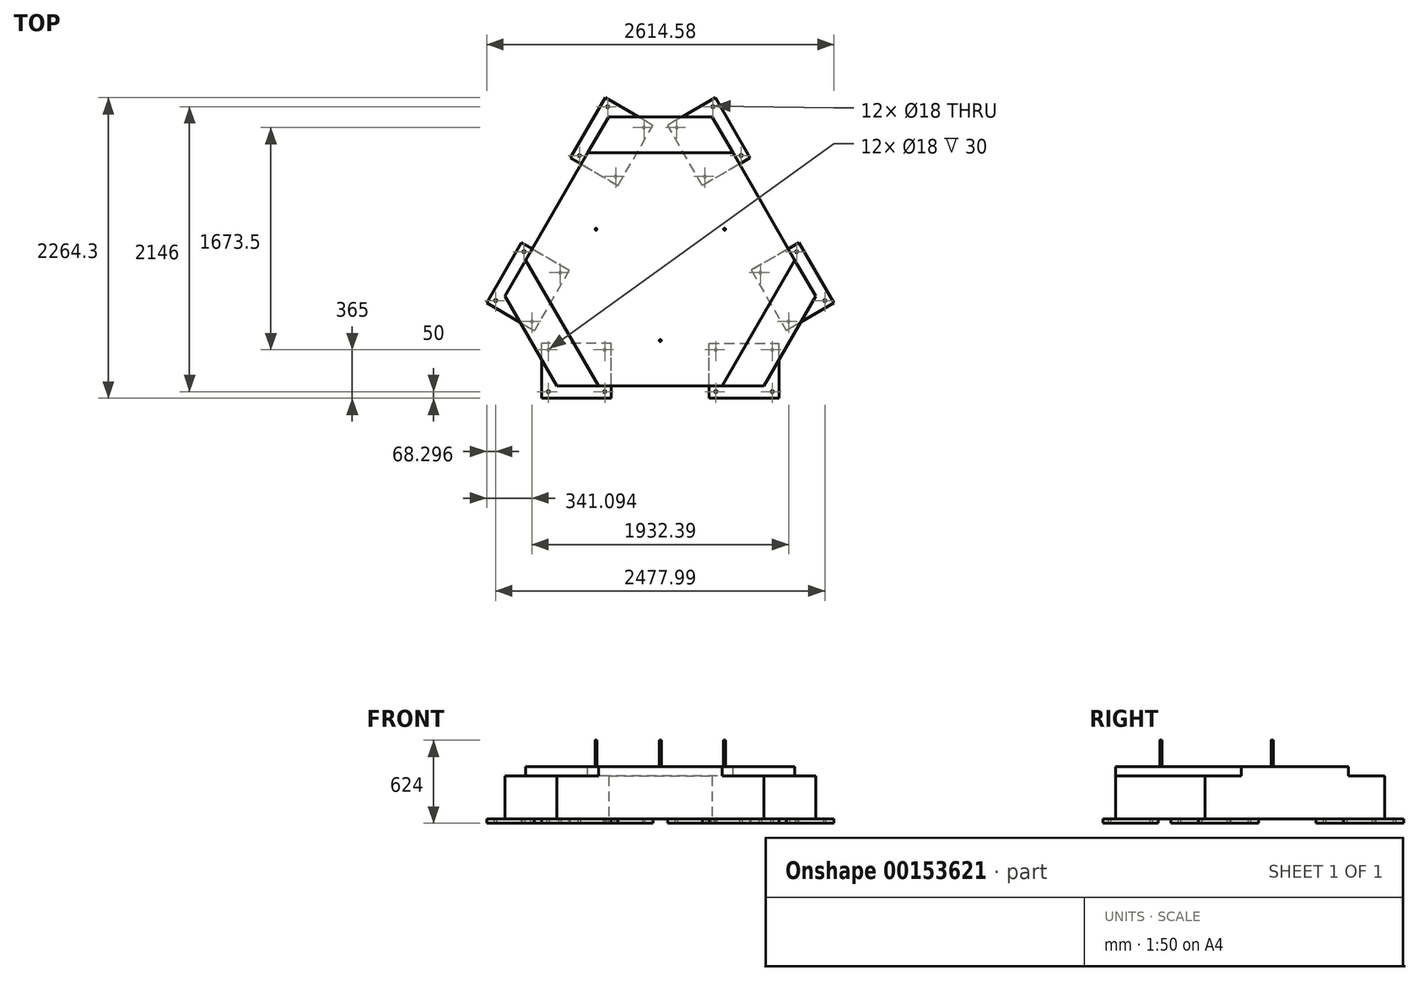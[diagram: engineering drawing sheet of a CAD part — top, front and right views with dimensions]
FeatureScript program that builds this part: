
annotation { "Feature Type Name" : "Feature", "Feature Type Description" : "" }
export const myFeature = defineFeature(function(context is Context, id is Id, definition is map)
    precondition{}
    {
        {
            var Q0;
            Q0=qCreatedBy(makeId("Top.planeOp"),FACE);
            var sketch = newSketch(context, id + "F0", { "sketchPlane" : qUnion([Q0])});
            skLineSegment(sketch, "E0", {"start": v(0, 1125.83) * mm, "end": v(390, 1125.83) * mm});
            skLineSegment(sketch, "E1", {"start": v(390, 1125.83) * mm, "end": v(780, 450.33) * mm});
            skLineSegment(sketch, "E2", {"start": v(0, 1304.98) * mm, "end": v(0, 0) * mm, "construction": true});
            skLineSegment(sketch, "E3", {"start": v(0, 0) * mm, "end": v(-698.78, -403.44) * mm, "construction": true});
            skLineSegment(sketch, "E4", {"start": v(0, 0) * mm, "end": v(965.92, -557.68) * mm, "construction": true});
            skLineSegment(sketch, "E5.MirrorCS", {"start": v(0, 1125.83) * mm, "end": v(-390, 1125.83) * mm});
            skLineSegment(sketch, "E6.MirrorCS", {"start": v(-390, 1125.83) * mm, "end": v(-780, 450.33) * mm});
            skLineSegment(sketch, "E7.MirrorCS", {"start": v(975, -562.92) * mm, "end": v(780, -900.67) * mm});
            skLineSegment(sketch, "E8.MirrorCS", {"start": v(975, -562.92) * mm, "end": v(1170, -225.17) * mm});
            skLineSegment(sketch, "E9.MirrorCS", {"start": v(1170, -225.17) * mm, "end": v(780, 450.33) * mm});
            skLineSegment(sketch, "E10.MirrorCS", {"start": v(780, -900.67) * mm, "end": v(0, -900.67) * mm});
            skLineSegment(sketch, "E11.MirrorCS", {"start": v(-975, -562.92) * mm, "end": v(-780, -900.67) * mm});
            skLineSegment(sketch, "E12.MirrorCS", {"start": v(-975, -562.92) * mm, "end": v(-1170, -225.17) * mm});
            skLineSegment(sketch, "E13.MirrorCS", {"start": v(-780, -900.67) * mm, "end": v(0, -900.67) * mm});
            skLineSegment(sketch, "E14.MirrorCS", {"start": v(-1170, -225.17) * mm, "end": v(-780, 450.33) * mm});
            skSolve(sketch);
        }
        {
            var Q0;
            Q0 = qSketchRegion(id + "F0", true);
            extrude(context, id + "F1", {"entities" : qUnion([Q0]), "depth" : 394 * mm});
        }
        {
            var Q0;
            Q0=makeQuery(id+"F1.opExtrude","CAP_FACE",FACE,{"disambiguationData":[OSD([sQuery(id+"F0.wireOp",EDGE,"E0"),sQuery(id+"F0.wireOp",EDGE,"E1"),sQuery(id+"F0.wireOp",EDGE,"E5.MirrorCS"),sQuery(id+"F0.wireOp",EDGE,"E6.MirrorCS"),sQuery(id+"F0.wireOp",EDGE,"E7.MirrorCS"),sQuery(id+"F0.wireOp",EDGE,"E8.MirrorCS"),sQuery(id+"F0.wireOp",EDGE,"E9.MirrorCS"),sQuery(id+"F0.wireOp",EDGE,"E10.MirrorCS"),sQuery(id+"F0.wireOp",EDGE,"E11.MirrorCS"),sQuery(id+"F0.wireOp",EDGE,"E12.MirrorCS"),sQuery(id+"F0.wireOp",EDGE,"E13.MirrorCS"),sQuery(id+"F0.wireOp",EDGE,"E14.MirrorCS")])],"isStart":false});
            var sketch = newSketch(context, id + "F2", { "sketchPlane" : qUnion([Q0])});
            skLineSegment(sketch, "E15", {"start": v(-390, 1125.83) * mm, "end": v(390, 1125.83) * mm});
            skLineSegment(sketch, "E16", {"start": v(390, 1125.83) * mm, "end": v(547, 853.9) * mm});
            skLineSegment(sketch, "E17", {"start": v(547, 853.9) * mm, "end": v(-547, 853.9) * mm});
            skLineSegment(sketch, "E18", {"start": v(-547, 853.9) * mm, "end": v(-390, 1125.83) * mm});
            skLineSegment(sketch, "E19", {"start": v(0, 1125.83) * mm, "end": v(0, 0) * mm, "construction": true});
            skLineSegment(sketch, "E20", {"start": v(-975, -562.92) * mm, "end": v(0, 0) * mm, "construction": true});
            skLineSegment(sketch, "E21", {"start": v(975, -562.92) * mm, "end": v(0, 0) * mm, "construction": true});
            skLineSegment(sketch, "E22.MirrorCS", {"start": v(1013, 46.77) * mm, "end": v(466, -900.67) * mm});
            skLineSegment(sketch, "E23.MirrorCS", {"start": v(466, -900.67) * mm, "end": v(780, -900.67) * mm});
            skLineSegment(sketch, "E24.MirrorCS", {"start": v(780, -900.67) * mm, "end": v(1170, -225.17) * mm});
            skLineSegment(sketch, "E25.MirrorCS", {"start": v(1170, -225.17) * mm, "end": v(1013, 46.77) * mm});
            skLineSegment(sketch, "E26.MirrorCS", {"start": v(-466, -900.67) * mm, "end": v(-1013, 46.77) * mm});
            skLineSegment(sketch, "E27.MirrorCS", {"start": v(-1013, 46.77) * mm, "end": v(-1170, -225.17) * mm});
            skLineSegment(sketch, "E28.MirrorCS", {"start": v(-1170, -225.17) * mm, "end": v(-780, -900.67) * mm});
            skLineSegment(sketch, "E29.MirrorCS", {"start": v(-780, -900.67) * mm, "end": v(-466, -900.67) * mm});
            skSolve(sketch);
        }
        {
            var Q0;
            Q0 = qSketchRegion(id + "F2", true);
            extrude(context, id + "F3", {"entities" : qUnion([Q0]), "operationType" : NewBodyOperationType.REMOVE, "oppositeDirection" : true, "depth" : 70 * mm});
        }
        {
            var Q0;
            Q0=makeQuery(id+"F1.opExtrude","CAP_FACE",FACE,{"disambiguationData":[OSD([sQuery(id+"F0.wireOp",EDGE,"E0"),sQuery(id+"F0.wireOp",EDGE,"E1"),sQuery(id+"F0.wireOp",EDGE,"E5.MirrorCS"),sQuery(id+"F0.wireOp",EDGE,"E6.MirrorCS"),sQuery(id+"F0.wireOp",EDGE,"E7.MirrorCS"),sQuery(id+"F0.wireOp",EDGE,"E8.MirrorCS"),sQuery(id+"F0.wireOp",EDGE,"E9.MirrorCS"),sQuery(id+"F0.wireOp",EDGE,"E10.MirrorCS"),sQuery(id+"F0.wireOp",EDGE,"E11.MirrorCS"),sQuery(id+"F0.wireOp",EDGE,"E12.MirrorCS"),sQuery(id+"F0.wireOp",EDGE,"E13.MirrorCS"),sQuery(id+"F0.wireOp",EDGE,"E14.MirrorCS")])],"isStart":true});
            var sketch = newSketch(context, id + "F4", { "sketchPlane" : qUnion([Q0])});
            skCircle(sketch, "E30", {"center": v(418, 943.96) * mm, "radius": 9 * mm});
            skLineSegment(sketch, "E31.bottom", {"start": v(368, 993.96) * mm, "end": v(893, 993.96) * mm});
            skLineSegment(sketch, "E31.top", {"start": v(368, 578.96) * mm, "end": v(893, 578.96) * mm});
            skLineSegment(sketch, "E31.left", {"start": v(368, 993.96) * mm, "end": v(368, 578.96) * mm});
            skLineSegment(sketch, "E31.right", {"start": v(893, 993.96) * mm, "end": v(893, 578.96) * mm});
            skPoint(sketch, "E31.middle", {"position": v(630.5, 786.46) * mm});
            skLineSegment(sketch, "E32", {"start": v(0, 900.67) * mm, "end": v(0, 0) * mm, "construction": true});
            skPoint(sketch, "E32.endSnap0", {"position": v(0, 900.67) * mm});
            skCircle(sketch, "E33", {"center": v(843, 943.96) * mm, "radius": 9 * mm});
            skLineSegment(sketch, "E34", {"start": v(843, 943.96) * mm, "end": v(418, 943.96) * mm, "construction": true});
            skCircle(sketch, "E35.MirrorC", {"center": v(-418, 943.96) * mm, "radius": 9 * mm});
            skCircle(sketch, "E36.MirrorC", {"center": v(-843, 943.96) * mm, "radius": 9 * mm});
            skLineSegment(sketch, "E37.MirrorCS", {"start": v(-368, 578.96) * mm, "end": v(-893, 578.96) * mm});
            skLineSegment(sketch, "E38.MirrorCS", {"start": v(-368, 993.96) * mm, "end": v(-368, 578.96) * mm});
            skLineSegment(sketch, "E39.MirrorCS", {"start": v(-368, 993.96) * mm, "end": v(-893, 993.96) * mm});
            skLineSegment(sketch, "E40.MirrorCS", {"start": v(-893, 993.96) * mm, "end": v(-893, 578.96) * mm});
            skLineSegment(sketch, "E41", {"start": v(630.5, 578.96) * mm, "end": v(630.5, 943.96) * mm, "construction": true});
            skLineSegment(sketch, "E42", {"start": v(368, 786.46) * mm, "end": v(893, 786.46) * mm, "construction": true});
            skCircle(sketch, "E43.MirrorC", {"center": v(843, 628.96) * mm, "radius": 9 * mm});
            skCircle(sketch, "E44.MirrorC", {"center": v(418, 628.96) * mm, "radius": 9 * mm});
            skCircle(sketch, "E45.MirrorC", {"center": v(-418, 628.96) * mm, "radius": 9 * mm});
            skCircle(sketch, "E46.MirrorC", {"center": v(-843, 628.96) * mm, "radius": 9 * mm});
            skLineSegment(sketch, "E47", {"start": v(418, 943.96) * mm, "end": v(418, 628.96) * mm, "construction": true});
            skLineSegment(sketch, "E48", {"start": v(780, -450.33) * mm, "end": v(0, 0) * mm, "construction": true});
            skLineSegment(sketch, "E49.MirrorCS", {"start": v(-317.4, -608.18) * mm, "end": v(-54.9, -1062.84) * mm});
            skLineSegment(sketch, "E50.MirrorCS", {"start": v(-676.8, -815.68) * mm, "end": v(-317.4, -608.18) * mm});
            skLineSegment(sketch, "E51.MirrorCS", {"start": v(-676.8, -815.68) * mm, "end": v(-414.3, -1270.34) * mm});
            skLineSegment(sketch, "E52.MirrorCS", {"start": v(-414.3, -1270.34) * mm, "end": v(-54.9, -1062.84) * mm});
            skLineSegment(sketch, "E53.MirrorCS", {"start": v(-685.4, 29.22) * mm, "end": v(-947.9, 483.88) * mm});
            skLineSegment(sketch, "E54.MirrorCS", {"start": v(-1044.8, -178.28) * mm, "end": v(-685.4, 29.22) * mm});
            skLineSegment(sketch, "E55.MirrorCS", {"start": v(-1307.3, 276.38) * mm, "end": v(-947.9, 483.88) * mm});
            skLineSegment(sketch, "E56.MirrorCS", {"start": v(-1044.8, -178.28) * mm, "end": v(-1307.3, 276.38) * mm});
            skCircle(sketch, "E57.MirrorC", {"center": v(-335.7, -676.48) * mm, "radius": 9 * mm});
            skCircle(sketch, "E58.MirrorC", {"center": v(-608.5, -833.98) * mm, "radius": 9 * mm});
            skCircle(sketch, "E59.MirrorC", {"center": v(-396, -1202.04) * mm, "radius": 9 * mm});
            skCircle(sketch, "E60.MirrorC", {"center": v(-1026.5, -109.98) * mm, "radius": 9 * mm});
            skCircle(sketch, "E61.MirrorC", {"center": v(-1239, 258.08) * mm, "radius": 9 * mm});
            skCircle(sketch, "E62.MirrorC", {"center": v(-966.2, 415.58) * mm, "radius": 9 * mm});
            skCircle(sketch, "E63.MirrorC", {"center": v(-753.7, 47.52) * mm, "radius": 9 * mm});
            skCircle(sketch, "E64.MirrorC", {"center": v(-123.2, -1044.54) * mm, "radius": 9 * mm});
            skLineSegment(sketch, "E65", {"start": v(-780, -450.33) * mm, "end": v(0, 0) * mm, "construction": true});
            skLineSegment(sketch, "E66.MirrorCS", {"start": v(317.4, -608.18) * mm, "end": v(54.9, -1062.84) * mm});
            skLineSegment(sketch, "E67.MirrorCS", {"start": v(414.3, -1270.34) * mm, "end": v(54.9, -1062.84) * mm});
            skLineSegment(sketch, "E68.MirrorCS", {"start": v(676.8, -815.68) * mm, "end": v(414.3, -1270.34) * mm});
            skLineSegment(sketch, "E69.MirrorCS", {"start": v(676.8, -815.68) * mm, "end": v(317.4, -608.18) * mm});
            skLineSegment(sketch, "E70.MirrorCS", {"start": v(685.4, 29.22) * mm, "end": v(947.9, 483.88) * mm});
            skLineSegment(sketch, "E71.MirrorCS", {"start": v(1307.3, 276.38) * mm, "end": v(947.9, 483.88) * mm});
            skLineSegment(sketch, "E72.MirrorCS", {"start": v(1044.8, -178.28) * mm, "end": v(685.4, 29.22) * mm});
            skLineSegment(sketch, "E73.MirrorCS", {"start": v(1044.8, -178.28) * mm, "end": v(1307.3, 276.38) * mm});
            skCircle(sketch, "E74.MirrorC", {"center": v(335.7, -676.48) * mm, "radius": 9 * mm});
            skCircle(sketch, "E75.MirrorC", {"center": v(123.2, -1044.54) * mm, "radius": 9 * mm});
            skCircle(sketch, "E76.MirrorC", {"center": v(396, -1202.04) * mm, "radius": 9 * mm});
            skCircle(sketch, "E77.MirrorC", {"center": v(608.5, -833.98) * mm, "radius": 9 * mm});
            skCircle(sketch, "E78.MirrorC", {"center": v(753.7, 47.52) * mm, "radius": 9 * mm});
            skCircle(sketch, "E79.MirrorC", {"center": v(966.2, 415.58) * mm, "radius": 9 * mm});
            skCircle(sketch, "E80.MirrorC", {"center": v(1239, 258.08) * mm, "radius": 9 * mm});
            skCircle(sketch, "E81.MirrorC", {"center": v(1026.5, -109.98) * mm, "radius": 9 * mm});
            skPoint(sketch, "E82.visualSharp", {"position": v(368, 993.96) * mm});
            skSolve(sketch);
        }
        {
            var Q0;
            Q0 = qSketchRegion(id + "F4", true);
            extrude(context, id + "F5", {"entities" : qUnion([Q0]), "operationType" : NewBodyOperationType.ADD, "depth" : 30 * mm});
        }
        {
            var Q0;
            Q0=makeQuery(id+"F1.opExtrude","CAP_FACE",FACE,{"disambiguationData":[OSD([sQuery(id+"F0.wireOp",EDGE,"E0"),sQuery(id+"F0.wireOp",EDGE,"E1"),sQuery(id+"F0.wireOp",EDGE,"E5.MirrorCS"),sQuery(id+"F0.wireOp",EDGE,"E6.MirrorCS"),sQuery(id+"F0.wireOp",EDGE,"E7.MirrorCS"),sQuery(id+"F0.wireOp",EDGE,"E8.MirrorCS"),sQuery(id+"F0.wireOp",EDGE,"E9.MirrorCS"),sQuery(id+"F0.wireOp",EDGE,"E10.MirrorCS"),sQuery(id+"F0.wireOp",EDGE,"E11.MirrorCS"),sQuery(id+"F0.wireOp",EDGE,"E12.MirrorCS"),sQuery(id+"F0.wireOp",EDGE,"E13.MirrorCS"),sQuery(id+"F0.wireOp",EDGE,"E14.MirrorCS")])],"isStart":false});
            var sketch = newSketch(context, id + "F6", { "sketchPlane" : qUnion([Q0])});
            skLineSegment(sketch, "E83", {"start": v(0, -900.67) * mm, "end": v(0, 0) * mm, "construction": true});
            skCircle(sketch, "E84", {"center": v(0, -559) * mm, "radius": 7.5 * mm});
            skCircle(sketch, "E85.0", {"center": v(-418, -943.96) * mm, "radius": 9 * mm, "construction": true});
            skCircle(sketch, "E86.0", {"center": v(418, -943.96) * mm, "radius": 9 * mm, "construction": true});
            skLineSegment(sketch, "E87", {"start": v(-418, -943.96) * mm, "end": v(418, -943.96) * mm, "construction": true});
            skLineSegment(sketch, "E88", {"start": v(-780, 450.33) * mm, "end": v(0, 0) * mm, "construction": true});
            skCircle(sketch, "E89", {"center": v(0, 0) * mm, "radius": 559 * mm, "construction": true});
            skCircle(sketch, "E90", {"center": v(-484.1, 279.5) * mm, "radius": 7.5 * mm});
            skLineSegment(sketch, "E91", {"start": v(0, 0) * mm, "end": v(780, 450.33) * mm, "construction": true});
            skCircle(sketch, "E92", {"center": v(484.1, 279.5) * mm, "radius": 7.5 * mm});
            skSolve(sketch);
        }
        {
            var Q0;
            Q0 = qSketchRegion(id + "F6", true);
            extrude(context, id + "F7", {"entities" : qUnion([Q0]), "operationType" : NewBodyOperationType.ADD, "depth" : 200 * mm});
        }
    });
